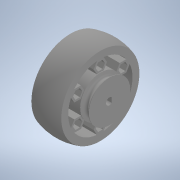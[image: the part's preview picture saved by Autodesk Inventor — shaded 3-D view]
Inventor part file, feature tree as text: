
AUTODESK INVENTOR PART (.ipt)
format: ipt  version: 2020 (Build 240168000, 168)  size: 365,568 bytes
history: native  units: in
note: dims shown in document units (in); Inventor stores cm internally (conversion verified against a paired STEP export)
features: sketch x4, extrude x2, revolve x2, projected_geometry x1
ambient origin geometry x8: Origin, YZ Plane, XZ Plane, XY Plane, X Axis, Y Axis, Z Axis, Center Point
bodies: Solid1 (feature_tree)
feature tree (9):
  extrude  "Extrusion1"  Depth=0.0394in
  sketch  "Sketch3"  dims[d6=0.7087in d7=0.1575in]
  revolve  "Revolution1"  [1 undecoded]
  extrude  "Extrusion2"  Depth=0.1575in
  revolve  "Revolution2"  [1 undecoded]
  sketch  "Sketch1"  dims[d0=0.1181in d1=0.0394in]
  sketch  "Sketch2"  dims[d3=1.3386in d4=0.1181in]
  projected_geometry  "Projected Loop1"
  sketch  "Sketch4"  dims[d8=0.0in d9=1.3386in d10=0.063in d11=0.0315in d12=2.3622in d14=360.0deg d16=0.5118in d17=0.0in d19=360.0deg d20=0.0787in d24=0.0394in d25=90.0deg d26=45.0deg d28=0.0079in]
note: 2 required parameter values undecoded (feature->parameter linkage not recoverable at this tier; creation-order binding heuristic only, values carry confidence <= 0.55)
